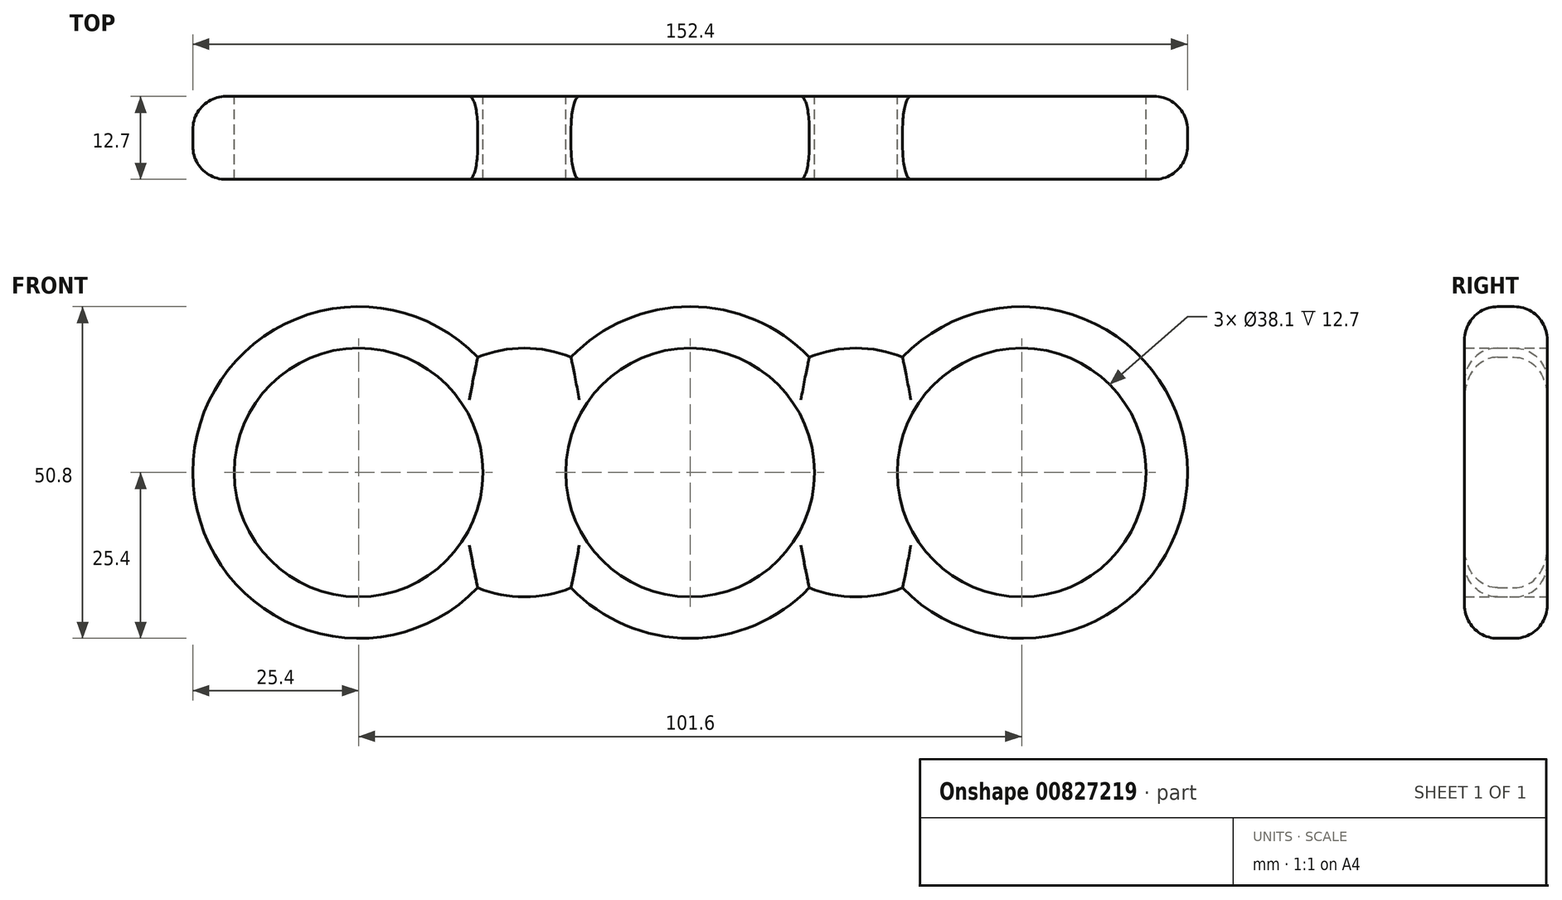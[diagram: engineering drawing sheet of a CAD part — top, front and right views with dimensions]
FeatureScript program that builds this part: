
annotation { "Feature Type Name" : "Feature", "Feature Type Description" : "" }
export const myFeature = defineFeature(function(context is Context, id is Id, definition is map)
    precondition{}
    {
        {
            var Q0;
            Q0=qCreatedBy(makeId("Front.planeOp"),FACE);
            var sketch = newSketch(context, id + "F0", { "sketchPlane" : qUnion([Q0])});
            skCircle(sketch, "E0", {"center": v(0, 0) * mm, "radius": 19.05 * mm});
            skCircle(sketch, "E1", {"center": v(-50.8, 0) * mm, "radius": 19.05 * mm});
            skCircle(sketch, "E2", {"center": v(50.8, 0) * mm, "radius": 19.05 * mm});
            skArc(sketch, "E3", {"start": v(-32.54, -17.66) * mm, "mid": v(-25.4, -19.05) * mm, "end": v(-18.26, -17.66) * mm});
            skArc(sketch, "E4", {"start": v(-18.26, 17.66) * mm, "mid": v(-25.4, 19.05) * mm, "end": v(-32.54, 17.66) * mm});
            skArc(sketch, "E5", {"start": v(18.26, -17.66) * mm, "mid": v(25.4, -19.05) * mm, "end": v(32.54, -17.66) * mm});
            skLineSegment(sketch, "E6", {"start": v(32.54, 17.66) * mm, "end": v(32.54, 17.66) * mm});
            skArc(sketch, "E7", {"start": v(32.54, 17.66) * mm, "mid": v(25.4, 19.05) * mm, "end": v(18.26, 17.66) * mm});
            skArc(sketch, "E8", {"start": v(32.54, -17.66) * mm, "mid": v(76.2, 0) * mm, "end": v(32.54, 17.66) * mm});
            skArc(sketch, "E9", {"start": v(18.26, 17.66) * mm, "mid": v(0, 25.4) * mm, "end": v(-18.26, 17.66) * mm});
            skArc(sketch, "E10", {"start": v(-18.26, -17.66) * mm, "mid": v(0, -25.4) * mm, "end": v(18.26, -17.66) * mm});
            skLineSegment(sketch, "E11", {"start": v(-32.54, 17.66) * mm, "end": v(-32.54, 17.66) * mm});
            skArc(sketch, "E12", {"start": v(-32.54, 17.66) * mm, "mid": v(-76.2, 0) * mm, "end": v(-32.54, -17.66) * mm});
            skSolve(sketch);
        }
        {
            var Q0;
            Q0=makeQuery(id+"F0.imprint","IMPRINT",FACE,{"disambiguationData":[TD([[makeQuery(id+"F0.imprint","IMPRINT",EDGE,{"derivedFrom":sQuery(id+"F0.wireOp",EDGE,"E0")}),-1.0]])]});
            extrude(context, id + "F1", {"entities" : qUnion([Q0]), "depth" : 12.7 * mm, "offsetDistance" : 25.4 * mm});
        }
        {
            var Q0;
            Q0=makeQuery(id+"F1.opExtrude","CAP_EDGE",EDGE,{"disambiguationData":[OSD([sQuery(id+"F0.wireOp",EDGE,"E12")])],"isStart":false});
            var Q1;
            Q1=makeQuery(id+"F1.opExtrude","CAP_EDGE",EDGE,{"disambiguationData":[OSD([sQuery(id+"F0.wireOp",EDGE,"E12")])],"isStart":true});
            var Q2;
            Q2=makeQuery(id+"F1.opExtrude","CAP_EDGE",EDGE,{"disambiguationData":[OSD([sQuery(id+"F0.wireOp",EDGE,"E4")])],"isStart":false});
            var Q3;
            Q3=makeQuery(id+"F1.opExtrude","CAP_EDGE",EDGE,{"disambiguationData":[OSD([sQuery(id+"F0.wireOp",EDGE,"E4")])],"isStart":true});
            var Q4;
            Q4=makeQuery(id+"F1.opExtrude","CAP_EDGE",EDGE,{"disambiguationData":[OSD([sQuery(id+"F0.wireOp",EDGE,"E9")])],"isStart":true});
            var Q5;
            Q5=makeQuery(id+"F1.opExtrude","CAP_EDGE",EDGE,{"disambiguationData":[OSD([sQuery(id+"F0.wireOp",EDGE,"E9")])],"isStart":false});
            var Q6;
            Q6=makeQuery(id+"F1.opExtrude","CAP_EDGE",EDGE,{"disambiguationData":[OSD([sQuery(id+"F0.wireOp",EDGE,"E7")])],"isStart":false});
            var Q7;
            Q7=makeQuery(id+"F1.opExtrude","CAP_EDGE",EDGE,{"disambiguationData":[OSD([sQuery(id+"F0.wireOp",EDGE,"E7")])],"isStart":true});
            var Q8;
            Q8=makeQuery(id+"F1.opExtrude","CAP_EDGE",EDGE,{"disambiguationData":[OSD([sQuery(id+"F0.wireOp",EDGE,"E8")])],"isStart":false});
            var Q9;
            Q9=makeQuery(id+"F1.opExtrude","CAP_EDGE",EDGE,{"disambiguationData":[OSD([sQuery(id+"F0.wireOp",EDGE,"E8")])],"isStart":true});
            var Q10;
            Q10=makeQuery(id+"F1.opExtrude","CAP_EDGE",EDGE,{"disambiguationData":[OSD([sQuery(id+"F0.wireOp",EDGE,"E3")])],"isStart":true});
            var Q11;
            Q11=makeQuery(id+"F1.opExtrude","CAP_EDGE",EDGE,{"disambiguationData":[OSD([sQuery(id+"F0.wireOp",EDGE,"E3")])],"isStart":false});
            var Q12;
            Q12=makeQuery(id+"F1.opExtrude","CAP_EDGE",EDGE,{"disambiguationData":[OSD([sQuery(id+"F0.wireOp",EDGE,"E10")])],"isStart":false});
            var Q13;
            Q13=makeQuery(id+"F1.opExtrude","CAP_EDGE",EDGE,{"disambiguationData":[OSD([sQuery(id+"F0.wireOp",EDGE,"E10")])],"isStart":true});
            var Q14;
            Q14=makeQuery(id+"F1.opExtrude","CAP_EDGE",EDGE,{"disambiguationData":[OSD([sQuery(id+"F0.wireOp",EDGE,"E5")])],"isStart":true});
            var Q15;
            Q15=makeQuery(id+"F1.opExtrude","CAP_EDGE",EDGE,{"disambiguationData":[OSD([sQuery(id+"F0.wireOp",EDGE,"E5")])],"isStart":false});
            fillet(context, id + "F2", {"entities" : qUnion([Q0, Q1, Q2, Q3, Q4, Q5, Q6, Q7, Q8, Q9, Q10, Q11, Q12, Q13, Q14, Q15]), "radius" : 5.08 * mm, "tangentPropagation" : true, "allowEdgeOverflow" : false});
        }
    });
